# Revit family: Haworth_BeHold_Accessory_StackOnShelf
name_source: partatom
category: Furniture Systems
revit_build: Autodesk Revit 2018 (Build: 20170223_1515(x64)
units: mm (PartAtom-declared; Revit-internal decimal feet)

## family parameters
Always vertical = Yes
Cut with Voids When Loaded = No
OmniClass Number = 23.40.70.14.64.21
OmniClass Title = Systems Furniture
Part Type = Normal
Room Calculation Point = No
Round Connector Dimension = Use Diameter
Shared = No
Work Plane-Based = No

## types (8) — shared parameters
Actual Height = 3/4"
Assembly Code = E2020200
Custom Size = No
Description = Haworth - Be_Hold - Accessory - Stack on Unit Shelf
Manufacturer = Haworth
Max. Depth = 24"
Max. Width = 36"
Min. Depth = 16"
Min. Width = 18"
Model = Haworth Be_Hold
Revision Number = 1
Shelf Edge Finish = Haworth _ Wood _ Maple H-AE
Shelf Finish = Haworth _ Wood _ Maple H-AE
Size = Verify Final Dim. w/ Haworth
Standard Depths = 16, 24 in.
Standard Widths = 18, 24, 30, 36 in.
Sustainability Info = https://www.haworth.com
Warranty = http://www.haworth.com

## per-type parameters (varying)
| type | Actual Depth | Actual Width | Depth | URL | URL - Product | Width |
| 16d 36w | 16" | 36" | 16" | http://www.haworth.com | http://www.haworth.com | 36" |
| 16d 30w | 16" | 30" | 16" | www.haworth.com |  | 30" |
| 16d 24w | 16" | 24" | 16" | www.haworth.com |  | 24" |
| 16d 18w | 16" | 18" | 16" | www.haworth.com |  | 18" |
| 24d 36w | 24" | 36" | 24" | http://www.haworth.com | http://www.haworth.com | 36" |
| 24d 30w | 24" | 30" | 24" | http://www.haworth.com | http://www.haworth.com | 30" |
| 24d 24w | 24" | 24" | 24" | http://www.haworth.com | http://www.haworth.com | 24" |
| 24d 18w | 24" | 18" | 24" | http://www.haworth.com | http://www.haworth.com | 18" |

## geometry (parser evidence)
native form markers: Sweep x2
no freeform markers — native parametric forms only
